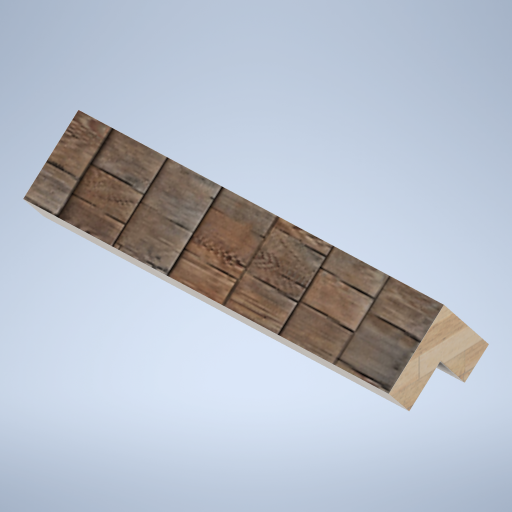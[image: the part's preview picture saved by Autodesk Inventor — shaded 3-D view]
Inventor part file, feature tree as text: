
AUTODESK INVENTOR PART (.ipt)
format: ipt  version: 2024.2 (Build 282272000, 272)  size: 506,368 bytes
history: native  units: mm
features: sketch x9, plane x5, extrude x4, loft x2, projected_geometry x2, other x1
ambient origin geometry x8: Origin, YZ Plane, XZ Plane, XY Plane, X Axis, Y Axis, Z Axis, Center Point
bodies: Solid1 (feature_tree)
feature tree (23):
  sketch  "Sketch1"  dims[d5=0.0mm d6=-8101.0mm d7=800.0mm]
  plane  "Work Plane2"
  loft  "Loft1"
  plane  "Work Plane3"
  extrude  "Extrusion1"  TaperAngle=0.0deg  [1 undecoded]
  sketch  "Sketch5"  dims[d15=6.981317mm d16=0.0mm d17=0.0mm]
  plane  "Work Plane4"
  extrude  "Extrusion2"  TaperAngle=0.0deg  [1 undecoded]
  plane  "Work Plane5"
  sketch  "Sketch7"  dims[d21=0.0mm d22=90.0deg d23=120.0mm]
  sketch  "Sketch8"  dims[d24=120.0mm]
  loft  "Loft2"
  extrude  "Extrusion3"  TaperAngle=0.0deg  [1 undecoded]
  extrude  "Extrusion4"  Depth=120.0mm
  plane  "Work Plane1"
  sketch  "Sketch2"  dims[d8=0.0mm d9=90.0deg d10=0.0mm d11=90.0deg]
  sketch  "Sketch3"  dims[d12=2600.0mm d13=0.0mm d14=0.0mm]
  sketch  "Sketch6"  dims[d18=90.0deg d19=0.0mm d20=90.0deg]
  projected_geometry  "Projected Loop1"
  projected_geometry  "Projected Loop2"
  other  "Edges1"
  sketch  "Sketch9"  dims[d25=100.0mm]
  sketch  "Sketch10"  dims[d26=100.0mm d27=1045.9mm d28=0.0mm d29=2000.0mm d30=0.0mm]
note: 3 required parameter values undecoded (feature->parameter linkage not recoverable at this tier; creation-order binding heuristic only, values carry confidence <= 0.55)
